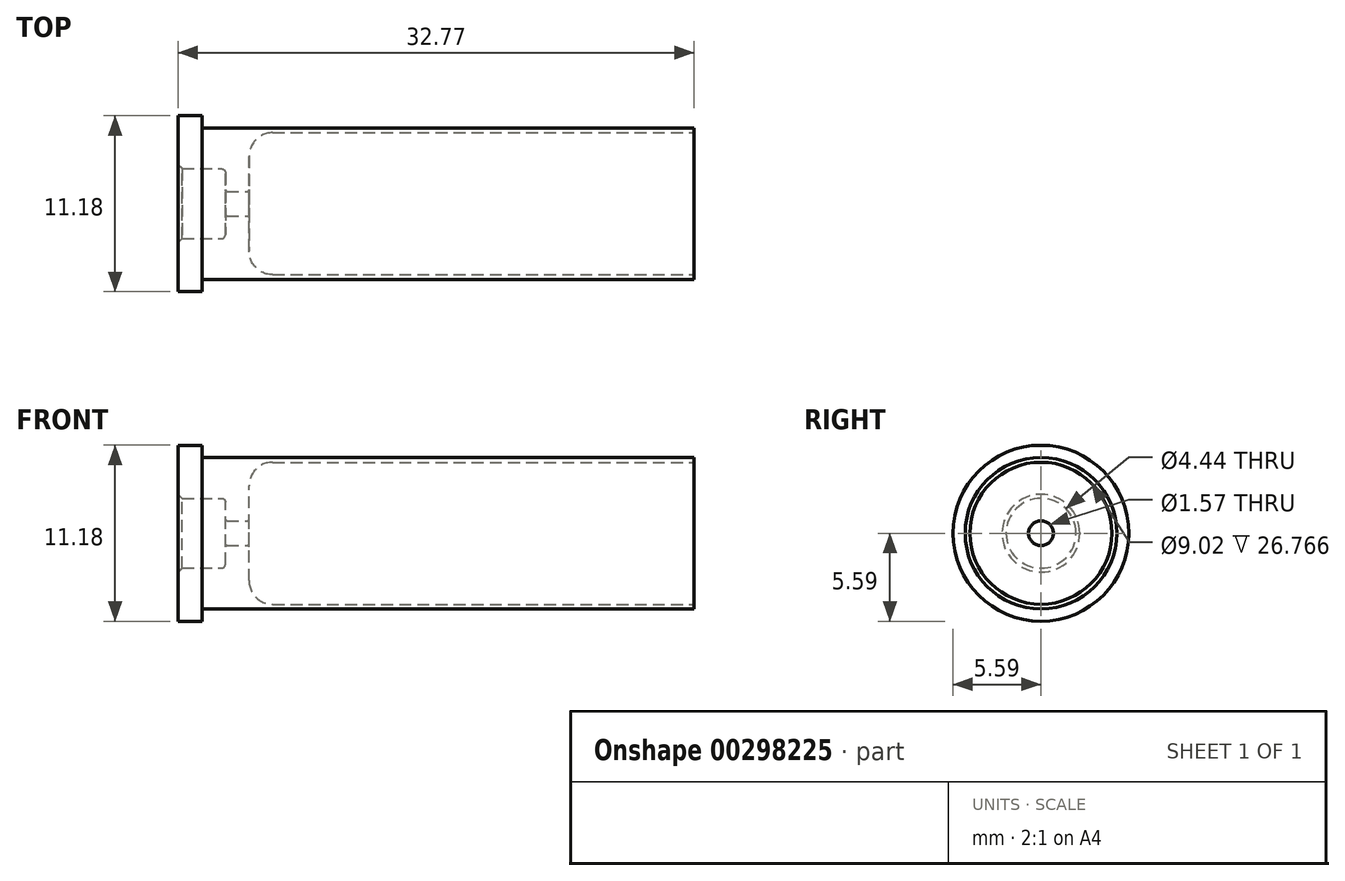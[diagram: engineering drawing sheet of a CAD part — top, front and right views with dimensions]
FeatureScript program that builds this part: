
annotation { "Feature Type Name" : "Feature", "Feature Type Description" : "" }
export const myFeature = defineFeature(function(context is Context, id is Id, definition is map)
    precondition{}
    {
        {
            var Q0;
            Q0=qCreatedBy(makeId("Top.planeOp"),FACE);
            var sketch = newSketch(context, id + "F0", { "sketchPlane" : qUnion([Q0])});
            skLineSegment(sketch, "E0", {"start": v(0, 2.22) * mm, "end": v(0, 5.59) * mm});
            skLineSegment(sketch, "E1", {"start": v(0, 5.59) * mm, "end": v(1.52, 5.59) * mm});
            skLineSegment(sketch, "E2", {"start": v(1.52, 5.59) * mm, "end": v(1.52, 4.81) * mm});
            skLineSegment(sketch, "E3", {"start": v(1.52, 4.81) * mm, "end": v(32.77, 4.81) * mm});
            skLineSegment(sketch, "E4", {"start": v(32.77, 4.81) * mm, "end": v(32.77, 4.5) * mm});
            skLineSegment(sketch, "E5", {"start": v(32.77, 0) * mm, "end": v(0, 0) * mm});
            skLineSegment(sketch, "E6", {"start": v(0, 2.22) * mm, "end": v(2.75, 2.22) * mm});
            skLineSegment(sketch, "E7", {"start": v(3.1, 0.79) * mm, "end": v(4.4, 0.79) * mm});
            skLineSegment(sketch, "E8", {"start": v(4.5, 0.89) * mm, "end": v(4.5, 3) * mm});
            skLineSegment(sketch, "E9", {"start": v(6, 4.5) * mm, "end": v(32.77, 4.5) * mm});
            skLineSegment(sketch, "E10", {"start": v(3, 1.97) * mm, "end": v(3, 0.89) * mm});
            skPoint(sketch, "E11.visualSharp", {"position": v(4.5, 4.5) * mm});
            skArc(sketch, "E11.filletArc", {"start": v(6, 4.5) * mm, "mid": v(4.94, 4.07) * mm, "end": v(4.5, 3) * mm});
            skPoint(sketch, "E12.visualSharp", {"position": v(3, 0.79) * mm});
            skArc(sketch, "E12.filletArc", {"start": v(3, 0.89) * mm, "mid": v(3.03, 0.82) * mm, "end": v(3.1, 0.79) * mm});
            skPoint(sketch, "E13.visualSharp", {"position": v(4.5, 0.79) * mm});
            skArc(sketch, "E13.filletArc", {"start": v(4.4, 0.79) * mm, "mid": v(4.47, 0.82) * mm, "end": v(4.5, 0.89) * mm});
            skPoint(sketch, "E14.visualSharp", {"position": v(3, 2.22) * mm});
            skArc(sketch, "E14.filletArc", {"start": v(3, 1.97) * mm, "mid": v(2.93, 2.15) * mm, "end": v(2.75, 2.22) * mm});
            skSolve(sketch);
        }
        {
            var Q0;
            Q0 = qSketchRegion(id + "F0", true);
            var Q1;
            Q1=sQuery(id+"F0.wireOp",EDGE,"E5");
            revolve(context, id + "F1", {"entities" : qUnion([Q0]), "axis" : qUnion([Q1]), "revolveType" : RevolveType.FULL});
        }
        {
            var Q0;
            Q0=makeQuery(id+"F1.opRevolve","SWEPT_EDGE",EDGE,{"disambiguationData":[OSD([sQuery(id+"F0.wireOp",EDGE,"E0"),sQuery(id+"F0.wireOp",EDGE,"E6")])]});
            chamfer(context, id + "F2", {"entities" : qUnion([Q0]), "width" : .25 * mm, "tangentPropagation" : true});
        }
    });
